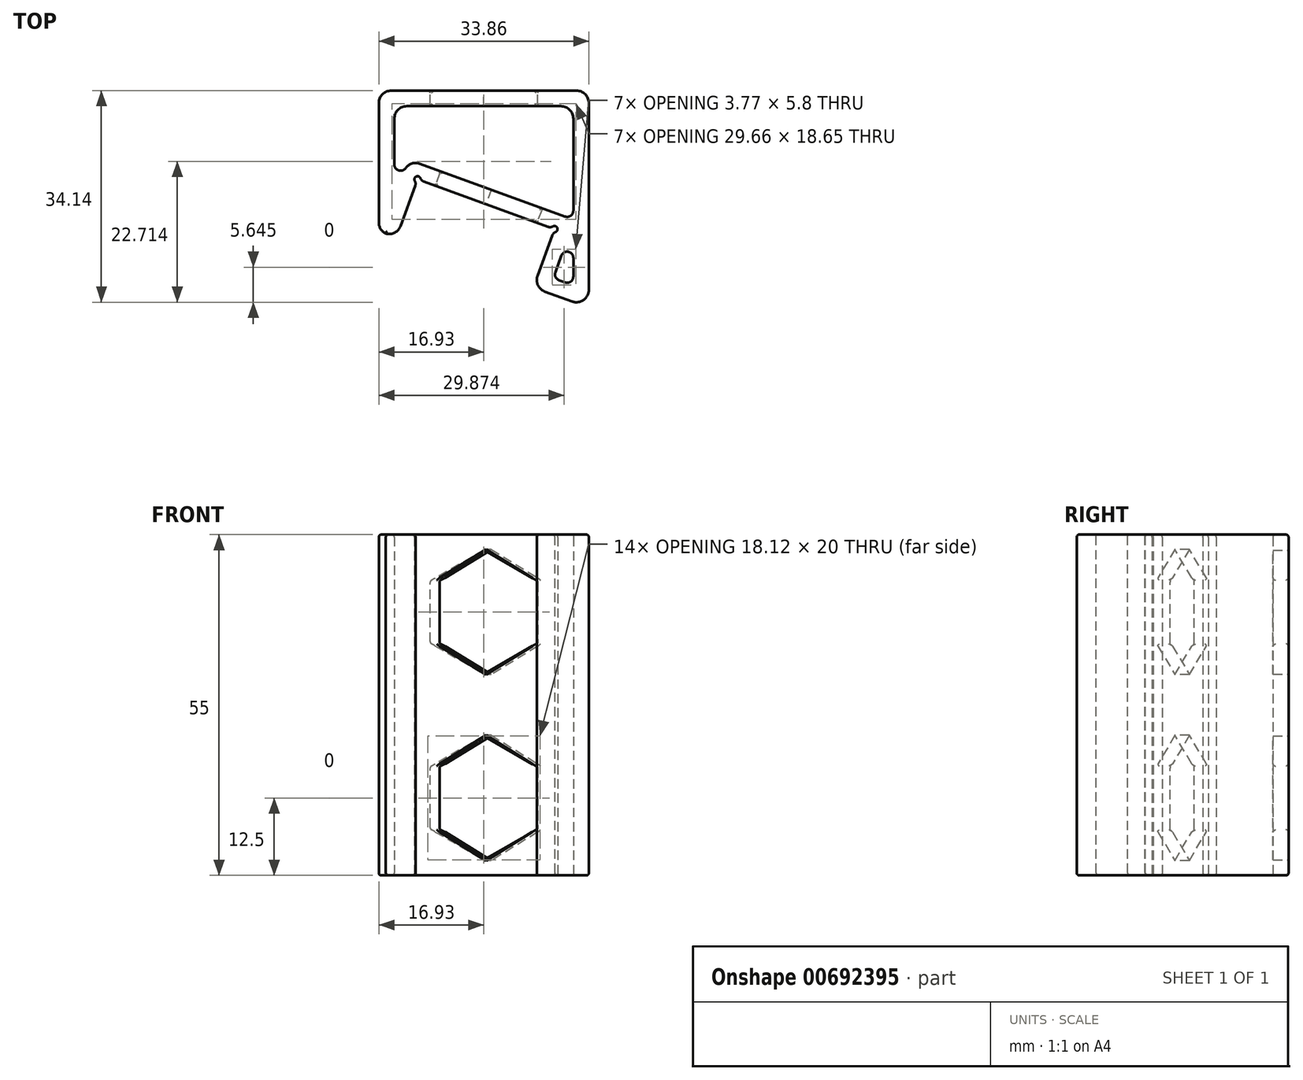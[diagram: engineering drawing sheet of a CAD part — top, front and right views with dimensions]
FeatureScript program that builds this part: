
annotation { "Feature Type Name" : "Feature", "Feature Type Description" : "" }
export const myFeature = defineFeature(function(context is Context, id is Id, definition is map)
    precondition{}
    {
        {
            var Q0;
            Q0=qCreatedBy(makeId("Right.planeOp"),FACE);
            var sketch = newSketch(context, id + "F0", { "sketchPlane" : qUnion([Q0])});
            skLineSegment(sketch, "E0", {"start": v(0, 0) * mm, "end": v(14.56, 0) * mm});
            skLineSegment(sketch, "E1", {"start": v(14.56, 0) * mm, "end": v(14.56, 40) * mm, "construction": true});
            skLineSegment(sketch, "E2", {"start": v(14.56, 40) * mm, "end": v(11.3, 31.04) * mm});
            skPoint(sketch, "E3", {"position": v(7.28, 20) * mm});
            skLineSegment(sketch, "E4", {"start": v(12.66, 5.54) * mm, "end": v(20.7, 27.62) * mm});
            skLineSegment(sketch, "E5", {"start": v(16.68, 16.58) * mm, "end": v(7.28, 20) * mm, "construction": true});
            skLineSegment(sketch, "E6", {"start": v(14.56, 0) * mm, "end": v(35, 0) * mm});
            skLineSegment(sketch, "E7", {"start": v(35, 0) * mm, "end": v(35, 40) * mm});
            skLineSegment(sketch, "E8", {"start": v(35, 40) * mm, "end": v(14.56, 40) * mm});
            skLineSegment(sketch, "E9", {"start": v(12.66, 5.54) * mm, "end": v(3.26, 8.96) * mm});
            skLineSegment(sketch, "E10", {"start": v(20.7, 27.62) * mm, "end": v(11.3, 31.04) * mm});
            skLineSegment(sketch, "E11", {"start": v(3.26, 8.96) * mm, "end": v(0, 0) * mm});
            skLineSegment(sketch, "E12", {"start": v(11.3, 31.04) * mm, "end": v(3.26, 8.96) * mm, "construction": true});
            skCircle(sketch, "E13", {"center": v(20.7, 27.62) * mm, "radius": 0.5 * mm});
            skCircle(sketch, "E14", {"center": v(12.66, 5.54) * mm, "radius": 0.5 * mm});
            skLineSegment(sketch, "E15", {"start": v(12.32, 33.86) * mm, "end": v(35, 33.86) * mm});
            skLineSegment(sketch, "E16.0", {"start": v(4.75, 5.75) * mm, "end": v(3.57, 2.5) * mm});
            skLineSegment(sketch, "E16.1", {"start": v(14.15, 2.33) * mm, "end": v(4.75, 5.75) * mm});
            skLineSegment(sketch, "E16.2", {"start": v(3.57, 2.5) * mm, "end": v(23.1, 2.5) * mm});
            skLineSegment(sketch, "E16.3", {"start": v(14.15, 2.33) * mm, "end": v(23.9, 29.12) * mm});
            skLineSegment(sketch, "E16.4", {"start": v(23.9, 29.12) * mm, "end": v(14.5, 32.54) * mm});
            skLineSegment(sketch, "E16.5", {"start": v(23.1, 2.5) * mm, "end": v(32.5, 2.5) * mm});
            skLineSegment(sketch, "E16.6", {"start": v(32.5, 2.5) * mm, "end": v(32.5, 37.5) * mm});
            skLineSegment(sketch, "E16.7", {"start": v(32.5, 37.5) * mm, "end": v(16.3, 37.5) * mm});
            skLineSegment(sketch, "E16.8", {"start": v(16.3, 37.5) * mm, "end": v(14.5, 32.54) * mm});
            skLineSegment(sketch, "E17", {"start": v(32.5, 31.36) * mm, "end": v(17.73, 31.36) * mm});
            skSolve(sketch);
        }
        {
            var Q0;
            Q0=makeQuery(id+"F0.imprint","IMPRINT",FACE,{"disambiguationData":[TD([[makeQuery(id+"F0.imprint","IMPRINT",EDGE,{"derivedFrom":sQuery(id+"F0.wireOp",EDGE,"E0")}),1.0]])]});
            var Q1;
            {var subQ0=sQuery(id+"F0.wireOp",EDGE,"E16.3");var subQ1=sQuery(id+"F0.wireOp",EDGE,"E16.1");var subQ2=makeQuery(id+"F0.imprint","INTERSECT",VERTEX,{"derivedFrom":[subQ1,subQ0]});Q1=makeQuery(id+"F0.imprint","IMPRINT",FACE,{"disambiguationData":[TD([[makeQuery(id+"F0.imprint","IMPRINT",EDGE,{"disambiguationData":[TD([[subQ2,-1.0]])],"derivedFrom":subQ1}),-1.0]])]});}
            var Q2;
            {var subQ5=sQuery(id+"F0.wireOp",EDGE,"E17");Q2=makeQuery(id+"F0.imprint","IMPRINT",FACE,{"disambiguationData":[TD([[makeQuery(id+"F0.imprint","IMPRINT",EDGE,{"derivedFrom":subQ5}),-1.0]])]});}
            extrude(context, id + "F1", {"entities" : qUnion([Q0, Q1, Q2]), "depth" : 25 * mm, "offsetDistance" : 25 * mm});
        }
        {
            var Q0;
            Q0=makeQuery(id+"F1.opExtrude","SWEPT_FACE",FACE,{"disambiguationData":[OSD([sQuery(id+"F0.wireOp",EDGE,"E4")])]});
            var sketch = newSketch(context, id + "F2", { "sketchPlane" : qUnion([Q0])});
            skPoint(sketch, "E18.0", {"position": v(12.5, 32.53) * mm});
            skPoint(sketch, "E18.1", {"position": v(0, 21.28) * mm});
            skLineSegment(sketch, "E19", {"start": v(0, 21.28) * mm, "end": v(22.76, 21.28) * mm, "construction": true});
            skLineSegment(sketch, "E20", {"start": v(12.5, 32.53) * mm, "end": v(12.5, 21.28) * mm, "construction": true});
            skCircle(sketch, "E21.cCircle", {"center": v(12.5, 21.28) * mm, "radius": 8.75 * mm, "construction": true});
            skLineSegment(sketch, "E21.0", {"start": v(7.45, 30.03) * mm, "end": v(17.55, 30.03) * mm});
            skLineSegment(sketch, "E21.1", {"start": v(17.55, 30.03) * mm, "end": v(22.6, 21.28) * mm});
            skLineSegment(sketch, "E21.2", {"start": v(22.6, 21.28) * mm, "end": v(17.55, 12.53) * mm});
            skLineSegment(sketch, "E21.3", {"start": v(17.55, 12.53) * mm, "end": v(7.45, 12.53) * mm});
            skLineSegment(sketch, "E21.4", {"start": v(7.45, 12.53) * mm, "end": v(2.4, 21.28) * mm});
            skLineSegment(sketch, "E21.5", {"start": v(2.4, 21.28) * mm, "end": v(7.45, 30.03) * mm});
            skPoint(sketch, "E21.0.midPoint", {"position": v(12.5, 30.03) * mm});
            skSolve(sketch);
        }
        {
            var Q0;
            Q0=makeQuery(id+"F2.imprint","IMPRINT",FACE,{"disambiguationData":[TD([[makeQuery(id+"F2.imprint","IMPRINT",EDGE,{"derivedFrom":sQuery(id+"F2.wireOp",EDGE,"E21.0")}),-1.0]])]});
            extrude(context, id + "F3", {"entities" : qUnion([Q0]), "operationType" : NewBodyOperationType.REMOVE, "oppositeDirection" : true, "depth" : 4.6 * mm, "offsetDistance" : 25 * mm});
        }
        {
            var Q0;
            Q0=makeQuery(id+"F1.opExtrude","SWEPT_FACE",FACE,{"disambiguationData":[OSD([sQuery(id+"F0.wireOp",EDGE,"E7")])]});
            var sketch = newSketch(context, id + "F4", { "sketchPlane" : qUnion([Q0])});
            skPoint(sketch, "E22.0", {"position": v(-12.5, 33.86) * mm});
            skPoint(sketch, "E22.1", {"position": v(-25, 16.93) * mm});
            skLineSegment(sketch, "E23", {"start": v(-25, 16.93) * mm, "end": v(-8.51, 16.93) * mm, "construction": true});
            skLineSegment(sketch, "E24", {"start": v(-12.5, 33.86) * mm, "end": v(-12.5, 16.93) * mm, "construction": true});
            skCircle(sketch, "E25.cCircle", {"center": v(-12.5, 16.93) * mm, "radius": 8.66 * mm, "construction": true});
            skLineSegment(sketch, "E25.0", {"start": v(-17.5, 25.6) * mm, "end": v(-7.5, 25.6) * mm});
            skLineSegment(sketch, "E25.1", {"start": v(-7.5, 25.6) * mm, "end": v(-2.5, 16.93) * mm});
            skLineSegment(sketch, "E25.2", {"start": v(-2.5, 16.93) * mm, "end": v(-7.5, 8.27) * mm});
            skLineSegment(sketch, "E25.3", {"start": v(-7.5, 8.27) * mm, "end": v(-17.5, 8.27) * mm});
            skLineSegment(sketch, "E25.4", {"start": v(-17.5, 8.27) * mm, "end": v(-22.5, 16.93) * mm});
            skLineSegment(sketch, "E25.5", {"start": v(-22.5, 16.93) * mm, "end": v(-17.5, 25.6) * mm});
            skPoint(sketch, "E25.0.midPoint", {"position": v(-12.5, 25.6) * mm});
            skSolve(sketch);
        }
        {
            var Q0;
            Q0=makeQuery(id+"F4.imprint","IMPRINT",FACE,{"disambiguationData":[TD([[makeQuery(id+"F4.imprint","IMPRINT",EDGE,{"derivedFrom":sQuery(id+"F4.wireOp",EDGE,"E25.0")}),-1.0]])]});
            extrude(context, id + "F5", {"entities" : qUnion([Q0]), "operationType" : NewBodyOperationType.REMOVE, "oppositeDirection" : true, "depth" : 4.8 * mm, "offsetDistance" : 25 * mm});
        }
        {
            var Q0;
            Q0=makeQuery(id+"F1.opExtrude","SWEPT_BODY",BODY,{"disambiguationData":[OSD([sQuery(id+"F0.wireOp",EDGE,"E0"),sQuery(id+"F0.wireOp",EDGE,"E2"),sQuery(id+"F0.wireOp",EDGE,"E4"),sQuery(id+"F0.wireOp",EDGE,"E6"),sQuery(id+"F0.wireOp",EDGE,"E7"),sQuery(id+"F0.wireOp",EDGE,"E9"),sQuery(id+"F0.wireOp",EDGE,"E10"),sQuery(id+"F0.wireOp",EDGE,"E11"),sQuery(id+"F0.wireOp",EDGE,"E13"),sQuery(id+"F0.wireOp",EDGE,"E14"),sQuery(id+"F0.wireOp",EDGE,"E15"),sQuery(id+"F0.wireOp",EDGE,"E16.0"),sQuery(id+"F0.wireOp",EDGE,"E16.1"),sQuery(id+"F0.wireOp",EDGE,"E16.2"),sQuery(id+"F0.wireOp",EDGE,"E16.3"),sQuery(id+"F0.wireOp",EDGE,"E16.4"),sQuery(id+"F0.wireOp",EDGE,"E16.5"),sQuery(id+"F0.wireOp",EDGE,"E16.6"),sQuery(id+"F0.wireOp",EDGE,"E17")])]});
            transform(context, id + "F6", {"entities" : qUnion([Q0]), "transformType" : TransformType.TRANSLATION_3D, "dx" : 30 * mm, "dy" : 0 * mm, "dz" : 0 * mm, "makeCopy" : true});
        }
        {
            var Q0;
            Q0=makeQuery(id+"F1.opExtrude","CAP_FACE",FACE,{"disambiguationData":[OSD([sQuery(id+"F0.wireOp",EDGE,"E0"),sQuery(id+"F0.wireOp",EDGE,"E2"),sQuery(id+"F0.wireOp",EDGE,"E4"),sQuery(id+"F0.wireOp",EDGE,"E6"),sQuery(id+"F0.wireOp",EDGE,"E7"),sQuery(id+"F0.wireOp",EDGE,"E9"),sQuery(id+"F0.wireOp",EDGE,"E10"),sQuery(id+"F0.wireOp",EDGE,"E11"),sQuery(id+"F0.wireOp",EDGE,"E13"),sQuery(id+"F0.wireOp",EDGE,"E14"),sQuery(id+"F0.wireOp",EDGE,"E15"),sQuery(id+"F0.wireOp",EDGE,"E16.0"),sQuery(id+"F0.wireOp",EDGE,"E16.1"),sQuery(id+"F0.wireOp",EDGE,"E16.2"),sQuery(id+"F0.wireOp",EDGE,"E16.3"),sQuery(id+"F0.wireOp",EDGE,"E16.4"),sQuery(id+"F0.wireOp",EDGE,"E16.5"),sQuery(id+"F0.wireOp",EDGE,"E16.6"),sQuery(id+"F0.wireOp",EDGE,"E17")])],"isStart":false});
            var Q1;
            Q1=makeQuery(id+"F6.opPattern","COPY",FACE,{"derivedFrom":makeQuery(id+"F1.opExtrude","CAP_FACE",FACE,{"disambiguationData":[OSD([sQuery(id+"F0.wireOp",EDGE,"E0"),sQuery(id+"F0.wireOp",EDGE,"E2"),sQuery(id+"F0.wireOp",EDGE,"E4"),sQuery(id+"F0.wireOp",EDGE,"E6"),sQuery(id+"F0.wireOp",EDGE,"E7"),sQuery(id+"F0.wireOp",EDGE,"E9"),sQuery(id+"F0.wireOp",EDGE,"E10"),sQuery(id+"F0.wireOp",EDGE,"E11"),sQuery(id+"F0.wireOp",EDGE,"E13"),sQuery(id+"F0.wireOp",EDGE,"E14"),sQuery(id+"F0.wireOp",EDGE,"E15"),sQuery(id+"F0.wireOp",EDGE,"E16.0"),sQuery(id+"F0.wireOp",EDGE,"E16.1"),sQuery(id+"F0.wireOp",EDGE,"E16.2"),sQuery(id+"F0.wireOp",EDGE,"E16.3"),sQuery(id+"F0.wireOp",EDGE,"E16.4"),sQuery(id+"F0.wireOp",EDGE,"E16.5"),sQuery(id+"F0.wireOp",EDGE,"E16.6"),sQuery(id+"F0.wireOp",EDGE,"E17")])],"isStart":true}),"instanceName":"1"});
            extrude(context, id + "F7", {"entities" : qUnion([Q0]), "operationType" : NewBodyOperationType.ADD, "endBound" : BoundingType.UP_TO_SURFACE, "depth" : 25 * mm, "endBoundEntityFace" : qUnion([Q1]), "offsetDistance" : 25 * mm});
        }
        {
            var Q0;
            Q0=makeQuery(id+"F1.opExtrude","SWEPT_EDGE",EDGE,{"disambiguationData":[OSD([sQuery(id+"F0.wireOp",EDGE,"E9"),sQuery(id+"F0.wireOp",EDGE,"E11")])]});
            var Q1;
            Q1=makeQuery(id+"F1.opExtrude","SWEPT_EDGE",EDGE,{"disambiguationData":[OSD([sQuery(id+"F0.wireOp",EDGE,"E2"),sQuery(id+"F0.wireOp",EDGE,"E10")])]});
            var Q2;
            Q2=makeQuery(id+"F1.opExtrude","SWEPT_EDGE",EDGE,{"disambiguationData":[OSD([sQuery(id+"F0.wireOp",EDGE,"E2"),sQuery(id+"F0.wireOp",EDGE,"E8")])]});
            var Q3;
            Q3=makeQuery(id+"F1.opExtrude","SWEPT_EDGE",EDGE,{"disambiguationData":[OSD([sQuery(id+"F0.wireOp",EDGE,"E7"),sQuery(id+"F0.wireOp",EDGE,"E8")])]});
            var Q4;
            Q4=makeQuery(id+"F1.opExtrude","SWEPT_EDGE",EDGE,{"disambiguationData":[OSD([sQuery(id+"F0.wireOp",EDGE,"E0"),sQuery(id+"F0.wireOp",EDGE,"E11")])]});
            var Q5;
            Q5=makeQuery(id+"F1.opExtrude","SWEPT_EDGE",EDGE,{"disambiguationData":[OSD([sQuery(id+"F0.wireOp",EDGE,"E6"),sQuery(id+"F0.wireOp",EDGE,"E7")])]});
            var Q6;
            Q6=makeQuery(id+"F1.opExtrude","SWEPT_EDGE",EDGE,{"disambiguationData":[OSD([sQuery(id+"F0.wireOp",EDGE,"E16.6"),sQuery(id+"F0.wireOp",EDGE,"E17")])]});
            var Q7;
            Q7=makeQuery(id+"F1.opExtrude","SWEPT_EDGE",EDGE,{"disambiguationData":[OSD([sQuery(id+"F0.wireOp",EDGE,"E16.5"),sQuery(id+"F0.wireOp",EDGE,"E16.6")])]});
            var Q8;
            Q8=makeQuery(id+"F1.opExtrude","SWEPT_EDGE",EDGE,{"disambiguationData":[OSD([sQuery(id+"F0.wireOp",EDGE,"E16.3"),sQuery(id+"F0.wireOp",EDGE,"E16.4")])]});
            fillet(context, id + "F8", {"entities" : qUnion([Q0, Q1, Q2, Q3, Q4, Q5, Q6, Q7, Q8]), "radius" : 2 * mm, "tangentPropagation" : true, "allowEdgeOverflow" : false});
        }
        {
            var Q0;
            Q0=makeQuery(id+"F1.opExtrude","SWEPT_EDGE",EDGE,{"disambiguationData":[OSD([sQuery(id+"F0.wireOp",EDGE,"E4"),sQuery(id+"F0.wireOp",EDGE,"E13")])]});
            var Q1;
            Q1=makeQuery(id+"F1.opExtrude","SWEPT_EDGE",EDGE,{"disambiguationData":[OSD([sQuery(id+"F0.wireOp",EDGE,"E10"),sQuery(id+"F0.wireOp",EDGE,"E13")])]});
            var Q2;
            Q2=makeQuery(id+"F1.opExtrude","SWEPT_EDGE",EDGE,{"disambiguationData":[OSD([sQuery(id+"F0.wireOp",EDGE,"E9"),sQuery(id+"F0.wireOp",EDGE,"E14")])]});
            var Q3;
            Q3=makeQuery(id+"F1.opExtrude","SWEPT_EDGE",EDGE,{"disambiguationData":[OSD([sQuery(id+"F0.wireOp",EDGE,"E4"),sQuery(id+"F0.wireOp",EDGE,"E14")])]});
            var Q4;
            Q4=makeQuery(id+"F1.opExtrude","SWEPT_EDGE",EDGE,{"disambiguationData":[OSD([sQuery(id+"F0.wireOp",EDGE,"E16.2"),sQuery(id+"F0.wireOp",EDGE,"E16.3")])]});
            var Q5;
            Q5=makeQuery(id+"F1.opExtrude","SWEPT_EDGE",EDGE,{"disambiguationData":[OSD([sQuery(id+"F0.wireOp",EDGE,"E16.4"),sQuery(id+"F0.wireOp",EDGE,"E17")])]});
            var Q6;
            Q6=makeQuery(id+"F1.opExtrude","SWEPT_EDGE",EDGE,{"disambiguationData":[OSD([sQuery(id+"F0.wireOp",EDGE,"E16.0"),sQuery(id+"F0.wireOp",EDGE,"E16.1")])]});
            var Q7;
            Q7=makeQuery(id+"F1.opExtrude","SWEPT_EDGE",EDGE,{"disambiguationData":[OSD([sQuery(id+"F0.wireOp",EDGE,"E16.1"),sQuery(id+"F0.wireOp",EDGE,"E16.2")])]});
            var Q8;
            Q8=makeQuery(id+"F1.opExtrude","SWEPT_EDGE",EDGE,{"disambiguationData":[OSD([sQuery(id+"F0.wireOp",EDGE,"E16.0"),sQuery(id+"F0.wireOp",EDGE,"E16.2")])]});
            fillet(context, id + "F9", {"entities" : qUnion([Q0, Q1, Q2, Q3, Q4, Q5, Q6, Q7, Q8]), "radius" : 1 * mm, "tangentPropagation" : true, "allowEdgeOverflow" : false});
        }
        {
            var Q0;
            Q0=makeQuery(id+"F1.opExtrude","CAP_EDGE",EDGE,{"disambiguationData":[OSD([sQuery(id+"F0.wireOp",EDGE,"E4")])],"isStart":false});
            var Q1;
            Q1=makeQuery(id+"F1.opExtrude","CAP_EDGE",EDGE,{"disambiguationData":[OSD([sQuery(id+"F0.wireOp",EDGE,"E4")])],"isStart":true});
            var Q2;
            Q2=makeQuery(id+"F1.opExtrude","CAP_EDGE",EDGE,{"disambiguationData":[OSD([sQuery(id+"F0.wireOp",EDGE,"E16.3")])],"isStart":false});
            var Q3;
            Q3=makeQuery(id+"F1.opExtrude","CAP_EDGE",EDGE,{"disambiguationData":[OSD([sQuery(id+"F0.wireOp",EDGE,"E16.0")])],"isStart":false});
            var Q4;
            Q4=makeQuery(id+"F1.opExtrude","CAP_EDGE",EDGE,{"disambiguationData":[OSD([sQuery(id+"F0.wireOp",EDGE,"E16.3")])],"isStart":true});
            var Q5;
            Q5=makeQuery(id+"F1.opExtrude","CAP_EDGE",EDGE,{"disambiguationData":[OSD([sQuery(id+"F0.wireOp",EDGE,"E16.1")])],"isStart":true});
            var Q6;
            Q6=makeQuery(id+"F3.boolean.opBoolean","COPY",FACE,{"derivedFrom":makeQuery(id+"F3.opExtrude","SWEPT_FACE",FACE,{"disambiguationData":[OSD([sQuery(id+"F2.wireOp",EDGE,"E21.3")])]})});
            var Q7;
            Q7=makeQuery(id+"F5.boolean.opBoolean","COPY",FACE,{"derivedFrom":makeQuery(id+"F5.opExtrude","SWEPT_FACE",FACE,{"disambiguationData":[OSD([sQuery(id+"F4.wireOp",EDGE,"E25.3")])]})});
            var Q8;
            Q8=makeQuery(id+"F5.boolean.opBoolean","COPY",FACE,{"derivedFrom":makeQuery(id+"F5.opExtrude","SWEPT_FACE",FACE,{"disambiguationData":[OSD([sQuery(id+"F4.wireOp",EDGE,"E25.0")])]})});
            var Q9;
            Q9=makeQuery(id+"F3.boolean.opBoolean","COPY",FACE,{"derivedFrom":makeQuery(id+"F3.opExtrude","SWEPT_FACE",FACE,{"disambiguationData":[OSD([sQuery(id+"F2.wireOp",EDGE,"E21.0")])]})});
            var Q10;
            Q10=makeQuery(id+"F6.opPattern","COPY",FACE,{"derivedFrom":makeQuery(id+"F3.boolean.opBoolean","COPY",FACE,{"derivedFrom":makeQuery(id+"F3.opExtrude","SWEPT_FACE",FACE,{"disambiguationData":[OSD([sQuery(id+"F2.wireOp",EDGE,"E21.3")])]})}),"instanceName":"1"});
            var Q11;
            Q11=makeQuery(id+"F6.opPattern","COPY",FACE,{"derivedFrom":makeQuery(id+"F5.boolean.opBoolean","COPY",FACE,{"derivedFrom":makeQuery(id+"F5.opExtrude","SWEPT_FACE",FACE,{"disambiguationData":[OSD([sQuery(id+"F4.wireOp",EDGE,"E25.3")])]})}),"instanceName":"1"});
            var Q12;
            Q12=makeQuery(id+"F6.opPattern","COPY",FACE,{"derivedFrom":makeQuery(id+"F5.boolean.opBoolean","COPY",FACE,{"derivedFrom":makeQuery(id+"F5.opExtrude","SWEPT_FACE",FACE,{"disambiguationData":[OSD([sQuery(id+"F4.wireOp",EDGE,"E25.0")])]})}),"instanceName":"1"});
            var Q13;
            Q13=makeQuery(id+"F6.opPattern","COPY",FACE,{"derivedFrom":makeQuery(id+"F3.boolean.opBoolean","COPY",FACE,{"derivedFrom":makeQuery(id+"F3.opExtrude","SWEPT_FACE",FACE,{"disambiguationData":[OSD([sQuery(id+"F2.wireOp",EDGE,"E21.0")])]})}),"instanceName":"1"});
            var Q14;
            Q14=makeQuery(id+"F6.opPattern","COPY",FACE,{"derivedFrom":makeQuery(id+"F1.opExtrude","CAP_FACE",FACE,{"disambiguationData":[OSD([sQuery(id+"F0.wireOp",EDGE,"E0"),sQuery(id+"F0.wireOp",EDGE,"E2"),sQuery(id+"F0.wireOp",EDGE,"E4"),sQuery(id+"F0.wireOp",EDGE,"E6"),sQuery(id+"F0.wireOp",EDGE,"E7"),sQuery(id+"F0.wireOp",EDGE,"E9"),sQuery(id+"F0.wireOp",EDGE,"E10"),sQuery(id+"F0.wireOp",EDGE,"E11"),sQuery(id+"F0.wireOp",EDGE,"E13"),sQuery(id+"F0.wireOp",EDGE,"E14"),sQuery(id+"F0.wireOp",EDGE,"E15"),sQuery(id+"F0.wireOp",EDGE,"E16.0"),sQuery(id+"F0.wireOp",EDGE,"E16.1"),sQuery(id+"F0.wireOp",EDGE,"E16.2"),sQuery(id+"F0.wireOp",EDGE,"E16.3"),sQuery(id+"F0.wireOp",EDGE,"E16.4"),sQuery(id+"F0.wireOp",EDGE,"E16.5"),sQuery(id+"F0.wireOp",EDGE,"E16.6"),sQuery(id+"F0.wireOp",EDGE,"E17")])],"isStart":false}),"instanceName":"1"});
            fillet(context, id + "F10", {"entities" : qUnion([Q0, Q1, Q2, Q3, Q4, Q5, Q6, Q7, Q8, Q9, Q10, Q11, Q12, Q13, Q14]), "radius" : 0.4 * mm, "tangentPropagation" : true, "allowEdgeOverflow" : false});
        }
        {
            var Q0;
            Q0=makeQuery(id+"F1.opExtrude","SWEPT_BODY",BODY,{"disambiguationData":[OSD([sQuery(id+"F0.wireOp",EDGE,"E0"),sQuery(id+"F0.wireOp",EDGE,"E2"),sQuery(id+"F0.wireOp",EDGE,"E4"),sQuery(id+"F0.wireOp",EDGE,"E6"),sQuery(id+"F0.wireOp",EDGE,"E7"),sQuery(id+"F0.wireOp",EDGE,"E9"),sQuery(id+"F0.wireOp",EDGE,"E10"),sQuery(id+"F0.wireOp",EDGE,"E11"),sQuery(id+"F0.wireOp",EDGE,"E13"),sQuery(id+"F0.wireOp",EDGE,"E14"),sQuery(id+"F0.wireOp",EDGE,"E15"),sQuery(id+"F0.wireOp",EDGE,"E16.0"),sQuery(id+"F0.wireOp",EDGE,"E16.1"),sQuery(id+"F0.wireOp",EDGE,"E16.2"),sQuery(id+"F0.wireOp",EDGE,"E16.3"),sQuery(id+"F0.wireOp",EDGE,"E16.4"),sQuery(id+"F0.wireOp",EDGE,"E16.5"),sQuery(id+"F0.wireOp",EDGE,"E16.6"),sQuery(id+"F0.wireOp",EDGE,"E17")])]});
            var Q1;
            {var subQ0=sQuery(id+"F0.wireOp",EDGE,"E6");var subQ1=sQuery(id+"F0.wireOp",EDGE,"E0");Q1=makeQuery(id+"F10.opFillet","BLEND_EDGE",EDGE,{"blendedFrom":[makeQuery(id+"F1.opExtrude","CAP_EDGE",EDGE,{"disambiguationData":[OSD([subQ1,subQ0])],"isStart":true}),makeQuery(id+"F1.opExtrude","SWEPT_FACE",FACE,{"disambiguationData":[OSD([subQ1,subQ0])]})],"blendedInto":[makeQuery(id+"F1.opExtrude","SWEPT_FACE",FACE,{"disambiguationData":[OSD([subQ1,subQ0])]})]});}
            transform(context, id + "F11", {"entities" : qUnion([Q0]), "transformType" : TransformType.ROTATION, "transformAxis" : qUnion([Q1]), "angle" : 90 * degree, "oppositeDirection" : true, "makeCopy" : false});
        }
    });
